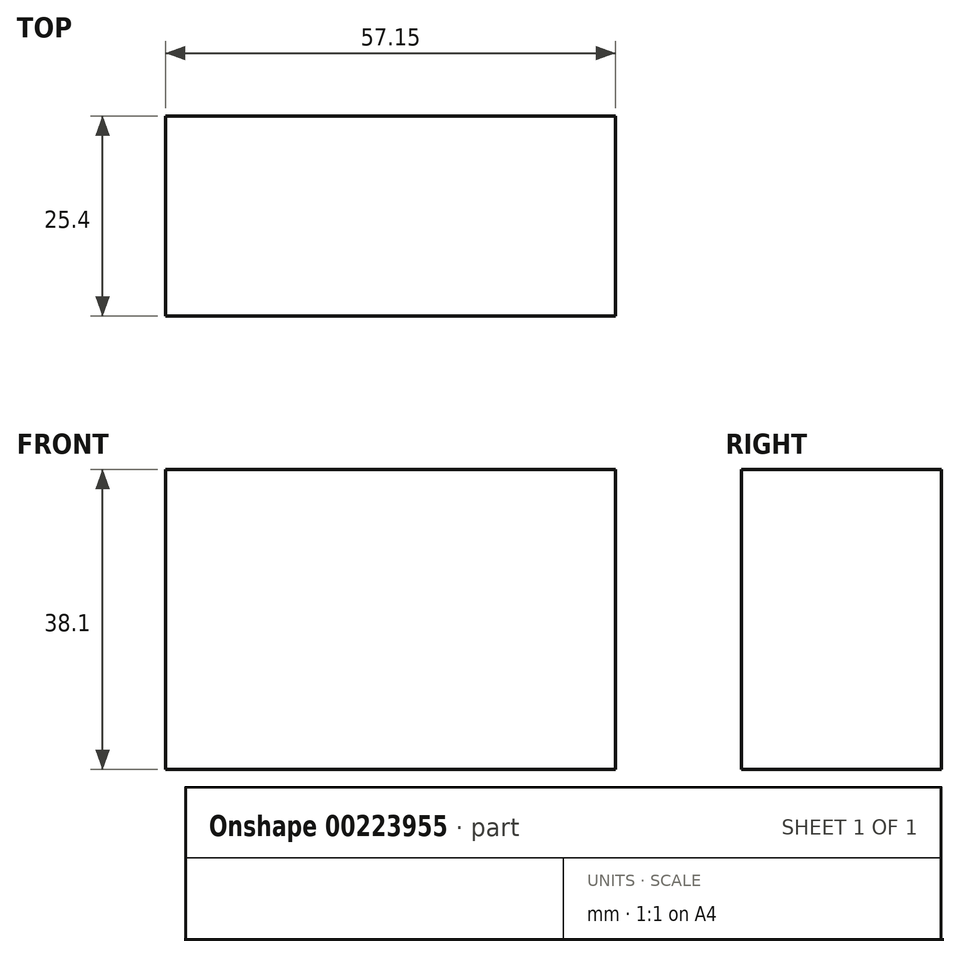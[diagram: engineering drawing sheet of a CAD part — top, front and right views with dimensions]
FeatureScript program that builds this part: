
annotation { "Feature Type Name" : "Feature", "Feature Type Description" : "" }
export const myFeature = defineFeature(function(context is Context, id is Id, definition is map)
    precondition{}
    {
        {
            var Q0;
            Q0=qCreatedBy(makeId("Front.planeOp"),FACE);
            var sketch = newSketch(context, id + "F0", { "sketchPlane" : qUnion([Q0])});
            skLineSegment(sketch, "E0.bottom", {"start": v(-36.41, 15.08) * mm, "end": v(-93.56, 15.08) * mm});
            skLineSegment(sketch, "E0.top", {"start": v(-36.41, 53.18) * mm, "end": v(-93.56, 53.18) * mm});
            skLineSegment(sketch, "E0.left", {"start": v(-36.41, 15.08) * mm, "end": v(-36.41, 53.18) * mm});
            skLineSegment(sketch, "E0.right", {"start": v(-93.56, 15.08) * mm, "end": v(-93.56, 53.18) * mm});
            skPoint(sketch, "E0.middle", {"position": v(-64.99, 34.13) * mm});
            skSolve(sketch);
        }
        {
            var Q0;
            Q0 = qSketchRegion(id + "F0", true);
            extrude(context, id + "F1", {"entities" : qUnion([Q0]), "endBound" : BoundingType.SYMMETRIC, "depth" : 25.4 * mm});
        }
    });
